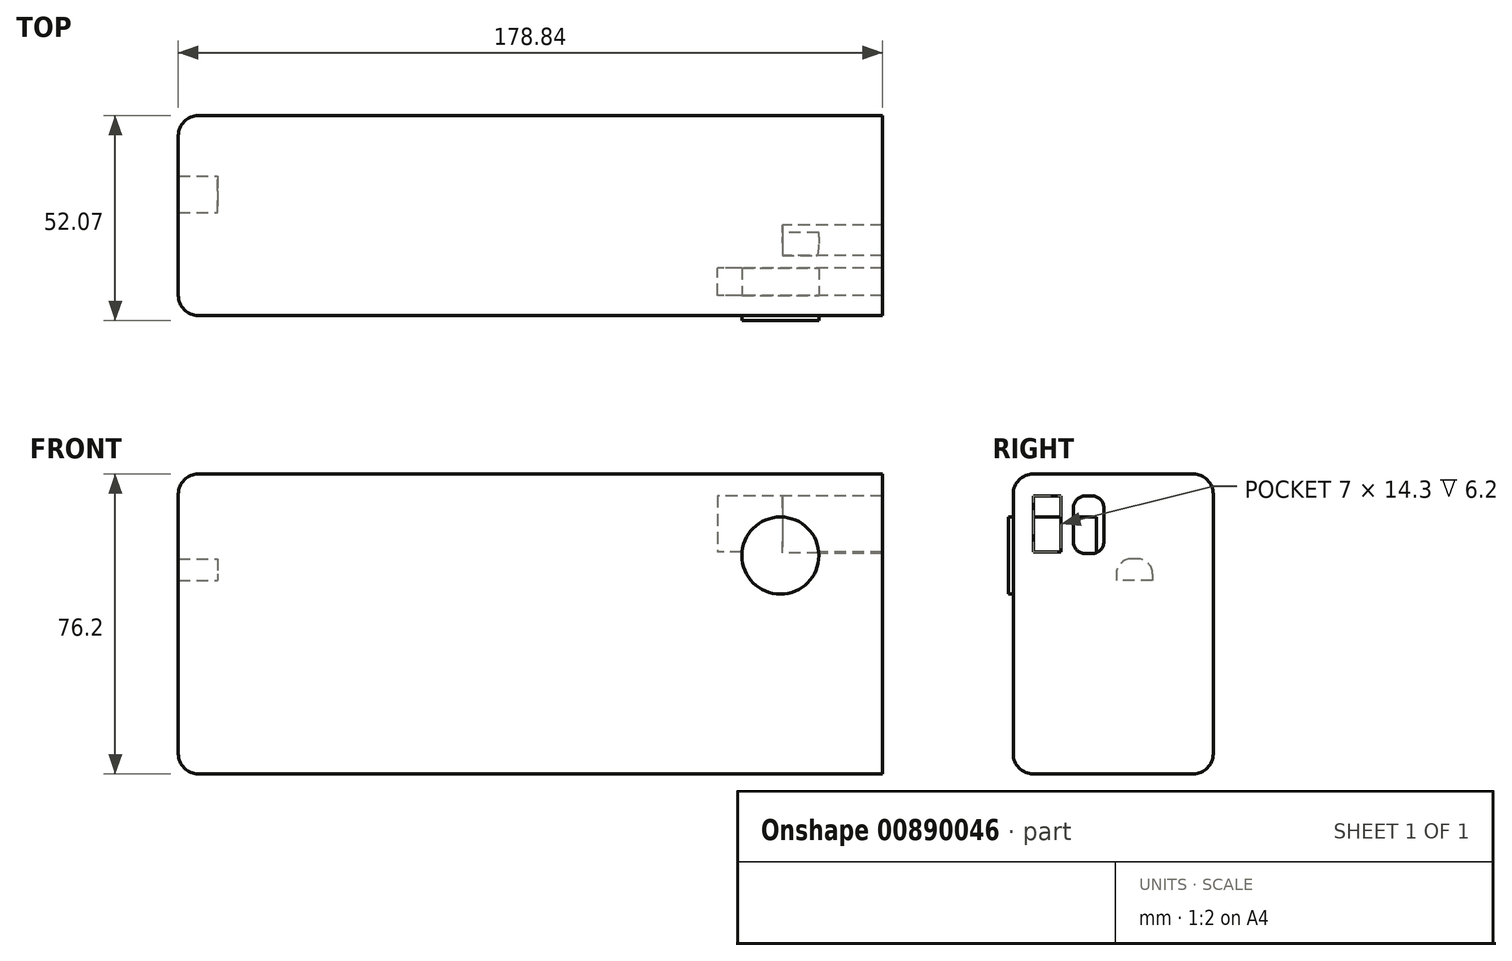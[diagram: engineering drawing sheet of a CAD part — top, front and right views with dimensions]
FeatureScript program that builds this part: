
annotation { "Feature Type Name" : "Feature", "Feature Type Description" : "" }
export const myFeature = defineFeature(function(context is Context, id is Id, definition is map)
    precondition{}
    {
        {
            var Q0;
            Q0=qCreatedBy(makeId("Front.planeOp"),FACE);
            var sketch = newSketch(context, id + "F0", { "sketchPlane" : qUnion([Q0])});
            skLineSegment(sketch, "E0.bottom", {"start": v(63.5, -38.1) * mm, "end": v(-63.5, -38.1) * mm});
            skLineSegment(sketch, "E0.top", {"start": v(63.5, 38.1) * mm, "end": v(-63.5, 38.1) * mm});
            skLineSegment(sketch, "E0.left", {"start": v(63.5, -38.1) * mm, "end": v(63.5, 38.1) * mm});
            skLineSegment(sketch, "E0.right", {"start": v(-63.5, -38.1) * mm, "end": v(-63.5, 38.1) * mm});
            skPoint(sketch, "E0.middle", {"position": v(0, 0) * mm});
            skSolve(sketch);
        }
        {
            var Q0;
            Q0=makeQuery(id+"F0.imprint","IMPRINT",FACE,{"disambiguationData":[TD([[makeQuery(id+"F0.imprint","IMPRINT",EDGE,{"derivedFrom":sQuery(id+"F0.wireOp",EDGE,"E0.bottom")}),-1.0]])]});
            extrude(context, id + "F1", {"entities" : qUnion([Q0]), "depth" : 50.8 * mm, "offsetDistance" : 25.4 * mm});
        }
        {
            var Q0;
            Q0=makeQuery(id+"F1.opExtrude","CAP_EDGE",EDGE,{"disambiguationData":[OSD([sQuery(id+"F0.wireOp",EDGE,"E0.top")])],"isStart":false});
            var Q1;
            Q1=makeQuery(id+"F1.opExtrude","CAP_EDGE",EDGE,{"disambiguationData":[OSD([sQuery(id+"F0.wireOp",EDGE,"E0.top")])],"isStart":true});
            var Q2;
            Q2=makeQuery(id+"F1.opExtrude","CAP_EDGE",EDGE,{"disambiguationData":[OSD([sQuery(id+"F0.wireOp",EDGE,"E0.bottom")])],"isStart":false});
            var Q3;
            Q3=makeQuery(id+"F1.opExtrude","CAP_EDGE",EDGE,{"disambiguationData":[OSD([sQuery(id+"F0.wireOp",EDGE,"E0.bottom")])],"isStart":true});
            fillet(context, id + "F2", {"entities" : qUnion([Q0, Q1, Q2, Q3]), "radius" : 5.08 * mm, "tangentPropagation" : true, "allowEdgeOverflow" : false});
        }
        {
            var Q0;
            Q0=makeQuery(id+"F1.opExtrude","SWEPT_FACE",FACE,{"disambiguationData":[OSD([sQuery(id+"F0.wireOp",EDGE,"E0.left")])]});
            var sketch = newSketch(context, id + "F3", { "sketchPlane" : qUnion([Q0])});
            skLineSegment(sketch, "E1.bottom", {"start": v(-45.72, 38.1) * mm, "end": v(-45.72, 38.1) * mm});
            skLineSegment(sketch, "E1.top", {"start": v(-45.72, 33.03) * mm, "end": v(-45.72, 33.03) * mm});
            skLineSegment(sketch, "E1.left", {"start": v(-45.72, 38.1) * mm, "end": v(-45.72, 33.03) * mm});
            skLineSegment(sketch, "E1.right", {"start": v(-45.72, 38.1) * mm, "end": v(-45.72, 33.03) * mm});
            skLineSegment(sketch, "E2.bottom", {"start": v(-45.72, 33.03) * mm, "end": v(-38.72, 33.03) * mm});
            skLineSegment(sketch, "E2.top", {"start": v(-45.72, 18.33) * mm, "end": v(-38.72, 18.33) * mm});
            skLineSegment(sketch, "E2.left", {"start": v(-45.72, 33.03) * mm, "end": v(-45.72, 18.33) * mm});
            skLineSegment(sketch, "E2.right", {"start": v(-38.72, 33.03) * mm, "end": v(-38.72, 18.33) * mm});
            skSolve(sketch);
        }
        {
            var Q0;
            Q0=makeQuery(id+"F3.imprint","IMPRINT",FACE,{"disambiguationData":[TD([[makeQuery(id+"F3.imprint","IMPRINT",EDGE,{"derivedFrom":sQuery(id+"F3.wireOp",EDGE,"E2.bottom")}),-1.0]])]});
            var Q1;
            Q1=makeQuery(id+"F3.imprint","IMPRINT",FACE,{"disambiguationData":[TD([[makeQuery(id+"F3.imprint","IMPRINT",EDGE,{"derivedFrom":sQuery(id+"F3.wireOp",EDGE,"E2.bottom")}),1.0]])]});
            extrude(context, id + "F4", {"entities" : qUnion([Q0, Q1]), "operationType" : NewBodyOperationType.ADD, "oppositeDirection" : true, "depth" : 16.4 * mm, "offsetDistance" : 25.4 * mm});
        }
        {
            var Q0;
            Q0=makeQuery(id+"F1.opExtrude","SWEPT_FACE",FACE,{"disambiguationData":[OSD([sQuery(id+"F0.wireOp",EDGE,"E0.left")])]});
            var sketch = newSketch(context, id + "F5", { "sketchPlane" : qUnion([Q0])});
            skLineSegment(sketch, "E3.bottom", {"start": v(-45.72, 32.56) * mm, "end": v(-38.72, 32.56) * mm});
            skLineSegment(sketch, "E3.top", {"start": v(-45.72, 18.26) * mm, "end": v(-38.72, 18.26) * mm});
            skLineSegment(sketch, "E3.left", {"start": v(-45.72, 32.56) * mm, "end": v(-45.72, 18.26) * mm});
            skLineSegment(sketch, "E3.right", {"start": v(-38.72, 32.56) * mm, "end": v(-38.72, 18.26) * mm});
            skSolve(sketch);
        }
        {
            var Q0;
            Q0=makeQuery(id+"F5.imprint","IMPRINT",FACE,{"disambiguationData":[TD([[makeQuery(id+"F5.imprint","IMPRINT",EDGE,{"derivedFrom":sQuery(id+"F5.wireOp",EDGE,"E3.bottom")}),1.0]])]});
            extrude(context, id + "F6", {"entities" : qUnion([Q0]), "operationType" : NewBodyOperationType.ADD, "depth" : 16.44 * mm, "offsetDistance" : 25.4 * mm});
        }
        {
            var Q0;
            Q0=makeQuery(id+"F6.opExtrude","CAP_FACE",FACE,{"disambiguationData":[OSD([sQuery(id+"F0.wireOp",EDGE,"E0.bottom"),sQuery(id+"F0.wireOp",EDGE,"E0.top"),sQuery(id+"F0.wireOp",EDGE,"E0.left"),sQuery(id+"F5.wireOp",EDGE,"E3.bottom"),sQuery(id+"F5.wireOp",EDGE,"E3.top"),sQuery(id+"F5.wireOp",EDGE,"E3.left"),sQuery(id+"F5.wireOp",EDGE,"E3.right")])],"isStart":false});
            var sketch = newSketch(context, id + "F7", { "sketchPlane" : qUnion([Q0])});
            skLineSegment(sketch, "E4", {"start": v(-35.54, 29.41) * mm, "end": v(-35.54, 20.91) * mm});
            skLineSegment(sketch, "E5", {"start": v(-32.5, 17.86) * mm, "end": v(-30.82, 17.86) * mm});
            skPoint(sketch, "E6.visualSharp", {"position": v(-35.54, 32.56) * mm});
            skArc(sketch, "E6.filletArc", {"start": v(-32.4, 32.56) * mm, "mid": v(-34.62, 31.64) * mm, "end": v(-35.54, 29.41) * mm});
            skPoint(sketch, "E7.visualSharp", {"position": v(-35.54, 17.86) * mm});
            skArc(sketch, "E7.filletArc", {"start": v(-35.54, 20.91) * mm, "mid": v(-34.65, 18.76) * mm, "end": v(-32.5, 17.86) * mm});
            skPoint(sketch, "E8.visualSharp", {"position": v(-27.77, 17.86) * mm});
            skArc(sketch, "E8.filletArc", {"start": v(-30.82, 17.86) * mm, "mid": v(-28.67, 18.76) * mm, "end": v(-27.77, 20.91) * mm});
            skLineSegment(sketch, "E9", {"start": v(-32.4, 32.56) * mm, "end": v(-30.82, 32.56) * mm});
            skLineSegment(sketch, "E10", {"start": v(-27.77, 29.51) * mm, "end": v(-27.77, 17.86) * mm});
            skPoint(sketch, "E11.visualSharp", {"position": v(-27.77, 32.56) * mm});
            skArc(sketch, "E11.filletArc", {"start": v(-27.77, 29.51) * mm, "mid": v(-28.67, 31.67) * mm, "end": v(-30.82, 32.56) * mm});
            skSolve(sketch);
        }
        {
            var Q0;
            Q0=makeQuery(id+"F7.imprint","IMPRINT",FACE,{"disambiguationData":[TD([[makeQuery(id+"F7.imprint","IMPRINT",EDGE,{"derivedFrom":sQuery(id+"F7.wireOp",EDGE,"E4")}),-1.0]])]});
            extrude(context, id + "F8", {"entities" : qUnion([Q0]), "operationType" : NewBodyOperationType.ADD, "depth" : 25.4 * mm, "offsetDistance" : 25.4 * mm});
        }
        {
            var Q0;
            {var subQ0=sQuery(id+"F0.wireOp",EDGE,"E0.left");var subQ1=makeQuery(id+"F5.imprint","IMPRINT",EDGE,{"derivedFrom":makeQuery(id+"F1.opExtrude","CAP_EDGE",EDGE,{"disambiguationData":[OSD([subQ0])],"isStart":false})});Q0=makeQuery(id+"F8.boolean.opBoolean","MERGE",FACE,{"derivedFrom":[makeQuery(id+"F6.boolean.opBoolean","MERGE",FACE,{"derivedFrom":[makeQuery(id+"F1.opExtrude","CAP_FACE",FACE,{"disambiguationData":[OSD([sQuery(id+"F0.wireOp",EDGE,"E0.bottom"),sQuery(id+"F0.wireOp",EDGE,"E0.top"),subQ0,sQuery(id+"F0.wireOp",EDGE,"E0.right")])],"isStart":false}),makeQuery(id+"F6.opExtrude","SWEPT_FACE",FACE,{"disambiguationData":[OSD([subQ0]),TDD([subQ1])]})]}),makeQuery(id+"F8.opExtrude","SWEPT_FACE",FACE,{"disambiguationData":[OSD([subQ0]),TDD([makeQuery(id+"F7.imprint","IMPRINT",EDGE,{"derivedFrom":makeQuery(id+"F6.opExtrude","CAP_EDGE",EDGE,{"disambiguationData":[OSD([subQ0]),TDD([subQ1])],"isStart":false})})])]})]});}
            var sketch = newSketch(context, id + "F9", { "sketchPlane" : qUnion([Q0])});
            skCircle(sketch, "E12", {"center": v(79.45, 17.39) * mm, "radius": 9.8 * mm});
            skCircle(sketch, "E13", {"center": v(93.82, 24.92) * mm, "radius": 3.65 * mm});
            skSolve(sketch);
        }
        {
            var Q0;
            Q0=makeQuery(id+"F9.imprint","IMPRINT",FACE,{"disambiguationData":[TD([[makeQuery(id+"F9.imprint","IMPRINT",EDGE,{"derivedFrom":sQuery(id+"F9.wireOp",EDGE,"E12")}),1.0]])]});
            extrude(context, id + "F10", {"entities" : qUnion([Q0]), "operationType" : NewBodyOperationType.ADD, "depth" : 1.27 * mm, "offsetDistance" : 25.4 * mm});
        }
        {
            var Q0;
            Q0=makeQuery(id+"F10.opExtrude","CAP_FACE",FACE,{"disambiguationData":[OSD([sQuery(id+"F9.wireOp",EDGE,"E12")])],"isStart":false});
            extrude(context, id + "F11", {"entities" : qUnion([Q0]), "operationType" : NewBodyOperationType.ADD, "oppositeDirection" : true, "depth" : 22.35 * mm, "offsetDistance" : 25.4 * mm});
        }
        {
            var Q0;
            Q0=makeQuery(id+"F1.opExtrude","SWEPT_FACE",FACE,{"disambiguationData":[OSD([sQuery(id+"F0.wireOp",EDGE,"E0.right")])]});
            var sketch = newSketch(context, id + "F12", { "sketchPlane" : qUnion([Q0])});
            skLineSegment(sketch, "E14", {"start": v(19.2, 16.55) * mm, "end": v(20.8, 16.55) * mm});
            skLineSegment(sketch, "E15", {"start": v(24.6, 12.74) * mm, "end": v(24.6, 11.08) * mm});
            skLineSegment(sketch, "E16", {"start": v(15.4, 12.74) * mm, "end": v(15.4, 11.08) * mm});
            skLineSegment(sketch, "E17", {"start": v(15.69, 11.08) * mm, "end": v(24.6, 11.08) * mm});
            skPoint(sketch, "E18.visualSharp", {"position": v(15.4, 16.55) * mm});
            skArc(sketch, "E18.filletArc", {"start": v(19.2, 16.55) * mm, "mid": v(16.51, 15.43) * mm, "end": v(15.4, 12.74) * mm});
            skPoint(sketch, "E19.visualSharp", {"position": v(24.6, 16.55) * mm});
            skArc(sketch, "E19.filletArc", {"start": v(24.6, 12.74) * mm, "mid": v(23.5, 15.43) * mm, "end": v(20.8, 16.55) * mm});
            skLineSegment(sketch, "E20", {"start": v(15.4, 11.08) * mm, "end": v(15.69, 11.08) * mm});
            skSolve(sketch);
        }
        {
            var Q0;
            Q0 = qSketchRegion(id + "F12", true);
            extrude(context, id + "F13", {"entities" : qUnion([Q0]), "operationType" : NewBodyOperationType.ADD, "oppositeDirection" : true, "depth" : 25.4 * mm, "offsetDistance" : 25.4 * mm});
        }
        {
            var Q0;
            Q0 = qSketchRegion(id + "F12", true);
            extrude(context, id + "F14", {"entities" : qUnion([Q0]), "operationType" : NewBodyOperationType.ADD, "oppositeDirection" : true, "depth" : 25.4 * mm, "offsetDistance" : 25.4 * mm});
        }
        {
            var Q0;
            Q0 = qSketchRegion(id + "F12", true);
            extrude(context, id + "F15", {"entities" : qUnion([Q0]), "operationType" : NewBodyOperationType.ADD, "oppositeDirection" : true, "depth" : 25.4 * mm, "offsetDistance" : 25.4 * mm});
        }
        {
            var Q0;
            Q0=makeQuery(id+"F12.imprint","IMPRINT",FACE,{"disambiguationData":[TD([[makeQuery(id+"F12.imprint","IMPRINT",EDGE,{"derivedFrom":sQuery(id+"F12.wireOp",EDGE,"E14")}),1.0]])]});
            extrude(context, id + "F16", {"entities" : qUnion([Q0]), "operationType" : NewBodyOperationType.ADD, "depth" : 10 * mm, "offsetDistance" : 25.4 * mm});
        }
        {
            var Q0;
            {var subQ0=sQuery(id+"F0.wireOp",EDGE,"E0.right");var subQ1=makeQuery(id+"F1.opExtrude","SWEPT_FACE",FACE,{"disambiguationData":[OSD([subQ0])]});var subQ2=sQuery(id+"F0.wireOp",EDGE,"E0.top");Q0=makeQuery(id+"F16.opExtrude","SWEPT_EDGE",EDGE,{"disambiguationData":[OSD([subQ2,subQ0]),TDD([makeQuery(id+"F12.imprint","INTERSECT",VERTEX,{"derivedFrom":[makeQuery(id+"FdgSTDokHU24AQQ_1.opFillet","BLEND_EDGE",EDGE,{"blendedFrom":[makeQuery(id+"F1.opExtrude","SWEPT_EDGE",EDGE,{"disambiguationData":[OSD([subQ2,subQ0])]}),subQ1],"blendedInto":[subQ1]}),makeQuery(id+"FdgSTDokHU24AQQ_1.opFillet","BLEND_EDGE",EDGE,{"blendedFrom":[makeQuery(id+"F1.opExtrude","CAP_EDGE",EDGE,{"disambiguationData":[OSD([subQ0])],"isStart":true}),subQ1],"blendedInto":[subQ1]})]})])]});}
            var Q1;
            {var subQ0=sQuery(id+"F0.wireOp",EDGE,"E0.right");var subQ1=sQuery(id+"F0.wireOp",EDGE,"E0.top");Q1=makeQuery(id+"F16.boolean.opBoolean","MERGE",EDGE,{"derivedFrom":[makeQuery(id+"FdgSTDokHU24AQQ_1.opFillet","BLEND_EDGE",EDGE,{"blendedFrom":[makeQuery(id+"F1.opExtrude","SWEPT_EDGE",EDGE,{"disambiguationData":[OSD([subQ1,subQ0])]}),makeQuery(id+"F1.opExtrude","SWEPT_FACE",FACE,{"disambiguationData":[OSD([subQ0])]})],"blendedInto":[makeQuery(id+"F1.opExtrude","SWEPT_FACE",FACE,{"disambiguationData":[OSD([subQ0])]})]}),makeQuery(id+"F16.opExtrude","CAP_EDGE",EDGE,{"disambiguationData":[OSD([subQ1,subQ0])],"isStart":true})]});}
            var Q2;
            {var subQ0=sQuery(id+"F0.wireOp",EDGE,"E0.right");var subQ1=makeQuery(id+"F1.opExtrude","SWEPT_FACE",FACE,{"disambiguationData":[OSD([subQ0])]});var subQ2=sQuery(id+"F0.wireOp",EDGE,"E0.top");Q2=makeQuery(id+"F16.opExtrude","SWEPT_EDGE",EDGE,{"disambiguationData":[OSD([subQ2,subQ0]),TDD([makeQuery(id+"F12.imprint","INTERSECT",VERTEX,{"derivedFrom":[makeQuery(id+"FdgSTDokHU24AQQ_1.opFillet","BLEND_EDGE",EDGE,{"blendedFrom":[makeQuery(id+"F1.opExtrude","SWEPT_EDGE",EDGE,{"disambiguationData":[OSD([subQ2,subQ0])]}),subQ1],"blendedInto":[subQ1]}),makeQuery(id+"FdgSTDokHU24AQQ_1.opFillet","BLEND_EDGE",EDGE,{"blendedFrom":[makeQuery(id+"F1.opExtrude","CAP_EDGE",EDGE,{"disambiguationData":[OSD([subQ0])],"isStart":false}),subQ1],"blendedInto":[subQ1]})]})])]});}
            var Q3;
            {var subQ0=sQuery(id+"F0.wireOp",EDGE,"E0.right");var subQ1=sQuery(id+"F0.wireOp",EDGE,"E0.top");Q3=makeQuery(id+"FdgSTDokHU24AQQ_1.opFillet","BLEND_FACE",FACE,{"disambiguationData":[OSD([subQ1,subQ0]),TDD([makeQuery(id+"F1.opExtrude","SWEPT_EDGE",EDGE,{"disambiguationData":[OSD([subQ1,subQ0])]})])]});}
            var Q4;
            Q4=makeQuery(id+"F16.opExtrude","CAP_EDGE",EDGE,{"disambiguationData":[OSD([sQuery(id+"F0.wireOp",EDGE,"E0.top"),sQuery(id+"F0.wireOp",EDGE,"E0.right")])],"isStart":false});
            var Q5;
            {var subQ0=sQuery(id+"F0.wireOp",EDGE,"E0.right");var subQ1=makeQuery(id+"FdgSTDokHU24AQQ_1.opFillet","BLEND_EDGE",EDGE,{"blendedFrom":[makeQuery(id+"F1.opExtrude","CAP_EDGE",EDGE,{"disambiguationData":[OSD([subQ0])],"isStart":true}),makeQuery(id+"F1.opExtrude","SWEPT_FACE",FACE,{"disambiguationData":[OSD([subQ0])]})],"blendedInto":[makeQuery(id+"F1.opExtrude","SWEPT_FACE",FACE,{"disambiguationData":[OSD([subQ0])]})]});Q5=makeQuery(id+"F16.boolean.opBoolean","MERGE",EDGE,{"derivedFrom":[subQ1,makeQuery(id+"F16.opExtrude","CAP_EDGE",EDGE,{"disambiguationData":[OSD([subQ0]),TDD([makeQuery(id+"F12.imprint","IMPRINT",EDGE,{"derivedFrom":subQ1})])],"isStart":true})]});}
            var Q6;
            {var subQ0=sQuery(id+"F0.wireOp",EDGE,"E0.right");Q6=makeQuery(id+"F16.opExtrude","CAP_EDGE",EDGE,{"disambiguationData":[OSD([subQ0]),TDD([makeQuery(id+"F12.imprint","IMPRINT",EDGE,{"derivedFrom":makeQuery(id+"FdgSTDokHU24AQQ_1.opFillet","BLEND_EDGE",EDGE,{"blendedFrom":[makeQuery(id+"F1.opExtrude","CAP_EDGE",EDGE,{"disambiguationData":[OSD([subQ0])],"isStart":true}),makeQuery(id+"F1.opExtrude","SWEPT_FACE",FACE,{"disambiguationData":[OSD([subQ0])]})],"blendedInto":[makeQuery(id+"F1.opExtrude","SWEPT_FACE",FACE,{"disambiguationData":[OSD([subQ0])]})]})})])],"isStart":false});}
            var Q7;
            {var subQ0=sQuery(id+"F0.wireOp",EDGE,"E0.right");Q7=makeQuery(id+"F16.opExtrude","CAP_EDGE",EDGE,{"disambiguationData":[OSD([subQ0]),TDD([makeQuery(id+"F12.imprint","IMPRINT",EDGE,{"derivedFrom":makeQuery(id+"FdgSTDokHU24AQQ_1.opFillet","BLEND_EDGE",EDGE,{"blendedFrom":[makeQuery(id+"F1.opExtrude","CAP_EDGE",EDGE,{"disambiguationData":[OSD([subQ0])],"isStart":false}),makeQuery(id+"F1.opExtrude","SWEPT_FACE",FACE,{"disambiguationData":[OSD([subQ0])]})],"blendedInto":[makeQuery(id+"F1.opExtrude","SWEPT_FACE",FACE,{"disambiguationData":[OSD([subQ0])]})]})})])],"isStart":false});}
            var Q8;
            {var subQ0=sQuery(id+"F0.wireOp",EDGE,"E0.right");var subQ1=makeQuery(id+"FdgSTDokHU24AQQ_1.opFillet","BLEND_EDGE",EDGE,{"blendedFrom":[makeQuery(id+"F1.opExtrude","CAP_EDGE",EDGE,{"disambiguationData":[OSD([subQ0])],"isStart":false}),makeQuery(id+"F1.opExtrude","SWEPT_FACE",FACE,{"disambiguationData":[OSD([subQ0])]})],"blendedInto":[makeQuery(id+"F1.opExtrude","SWEPT_FACE",FACE,{"disambiguationData":[OSD([subQ0])]})]});Q8=makeQuery(id+"F16.boolean.opBoolean","MERGE",EDGE,{"derivedFrom":[subQ1,makeQuery(id+"F16.opExtrude","CAP_EDGE",EDGE,{"disambiguationData":[OSD([subQ0]),TDD([makeQuery(id+"F12.imprint","IMPRINT",EDGE,{"derivedFrom":subQ1})])],"isStart":true})]});}
            var Q9;
            Q9=makeQuery(id+"F16.opExtrude","CAP_EDGE",EDGE,{"disambiguationData":[OSD([sQuery(id+"F0.wireOp",EDGE,"E0.bottom"),sQuery(id+"F0.wireOp",EDGE,"E0.right")])],"isStart":false});
            var Q10;
            {var subQ0=sQuery(id+"F0.wireOp",EDGE,"E0.right");var subQ1=sQuery(id+"F0.wireOp",EDGE,"E0.bottom");Q10=makeQuery(id+"F16.boolean.opBoolean","MERGE",EDGE,{"derivedFrom":[makeQuery(id+"FdgSTDokHU24AQQ_1.opFillet","BLEND_EDGE",EDGE,{"blendedFrom":[makeQuery(id+"F1.opExtrude","SWEPT_EDGE",EDGE,{"disambiguationData":[OSD([subQ1,subQ0])]}),makeQuery(id+"F1.opExtrude","SWEPT_FACE",FACE,{"disambiguationData":[OSD([subQ0])]})],"blendedInto":[makeQuery(id+"F1.opExtrude","SWEPT_FACE",FACE,{"disambiguationData":[OSD([subQ0])]})]}),makeQuery(id+"F16.opExtrude","CAP_EDGE",EDGE,{"disambiguationData":[OSD([subQ1,subQ0])],"isStart":true})]});}
            var Q11;
            {var subQ0=sQuery(id+"F0.wireOp",EDGE,"E0.right");var subQ1=makeQuery(id+"F1.opExtrude","SWEPT_FACE",FACE,{"disambiguationData":[OSD([subQ0])]});var subQ2=sQuery(id+"F0.wireOp",EDGE,"E0.bottom");Q11=makeQuery(id+"F16.opExtrude","SWEPT_EDGE",EDGE,{"disambiguationData":[OSD([subQ2,subQ0]),TDD([makeQuery(id+"F12.imprint","INTERSECT",VERTEX,{"derivedFrom":[makeQuery(id+"FdgSTDokHU24AQQ_1.opFillet","BLEND_EDGE",EDGE,{"blendedFrom":[makeQuery(id+"F1.opExtrude","SWEPT_EDGE",EDGE,{"disambiguationData":[OSD([subQ2,subQ0])]}),subQ1],"blendedInto":[subQ1]}),makeQuery(id+"FdgSTDokHU24AQQ_1.opFillet","BLEND_EDGE",EDGE,{"blendedFrom":[makeQuery(id+"F1.opExtrude","CAP_EDGE",EDGE,{"disambiguationData":[OSD([subQ0])],"isStart":true}),subQ1],"blendedInto":[subQ1]})]})])]});}
            fillet(context, id + "F17", {"entities" : qUnion([Q0, Q1, Q2, Q3, Q4, Q5, Q6, Q7, Q8, Q9, Q10, Q11]), "radius" : 5.08 * mm, "tangentPropagation" : true, "allowEdgeOverflow" : false});
        }
    });
